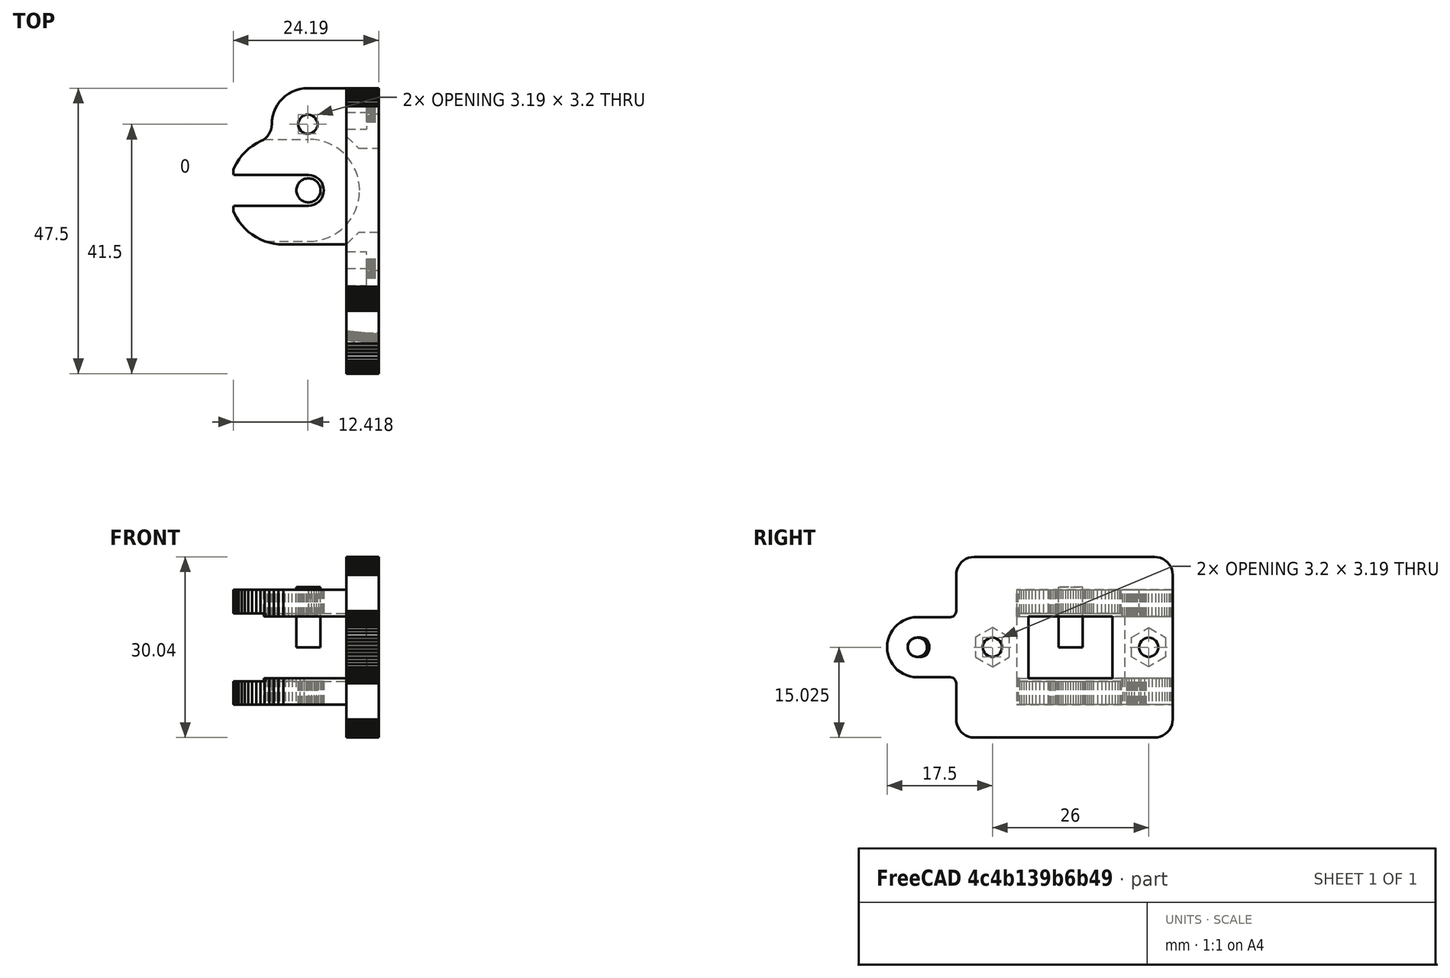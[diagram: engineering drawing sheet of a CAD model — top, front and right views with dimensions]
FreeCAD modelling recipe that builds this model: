
FCSTD DOCUMENT  (FreeCAD 0.18R14555 (Git shallow))
Label: y-roller-base
License: All rights reserved
LicenseURL: http://en.wikipedia.org/wiki/All_rights_reserved
objects: Part::Feature×3, Part::Cylinder×2, Mesh::Feature×1, Part::Box×1, Part::MultiFuse×1, Part::Cut×1, Part::Chamfer×1
note: 9 computed .brp shape members not serialized (recipe doc carries the construction recipe); baked Part::Feature solids carry a one-line shape summary decoded from their .brp

FEATURE [Mesh::Feature] base
FEATURE [Part::Feature] base001
  shape: bbox 24.19 x 47.5 x 30.04 mm, 2998 faces, 0 solids (baked)
FEATURE [Part::Feature] base001001  label="base002"
  shape: bbox 24.19 x 47.5 x 30.04 mm, 1760 faces, 0 solids (baked)
FEATURE [Part::Feature] base001001_solid  label="base002 (Solid)"
  shape: bbox 24.19 x 47.5 x 30.04 mm, 1760 faces (baked)
FEATURE [Part::Cylinder] Cylinder
  Angle = 360
  AttacherType = Attacher::AttachEngine3D
  Height = 11.3
  Placement = pos=(-9,0,-5.65) rot=(0,0,1;0rad)
  Radius = 8.5
FEATURE [Part::Cylinder] Cylinder001
  Angle = 360
  AttacherType = Attacher::AttachEngine3D
  Height = 10
  Placement = pos=(-9,0,0) rot=(0,0,1;0rad)
  Radius = 2
FEATURE [Part::Box] Box  label="Cube"
  AttacherType = Attacher::AttachEngine3D
  Height = 11.3
  Length = 17
  Placement = pos=(-26,-8.5,-5.65) rot=(0,0,1;0rad)
  Width = 17
FEATURE [Part::MultiFuse] Fusion
  Shapes = -> [Cylinder,Box]
FEATURE [Part::Cut] Cut
  Base = -> base001001_solid
  Tool = -> Fusion
FEATURE [Part::Chamfer] Chamfer
  Base = -> Cut
  Edges = 2 edges r=2: [Edge259,Edge1049]
